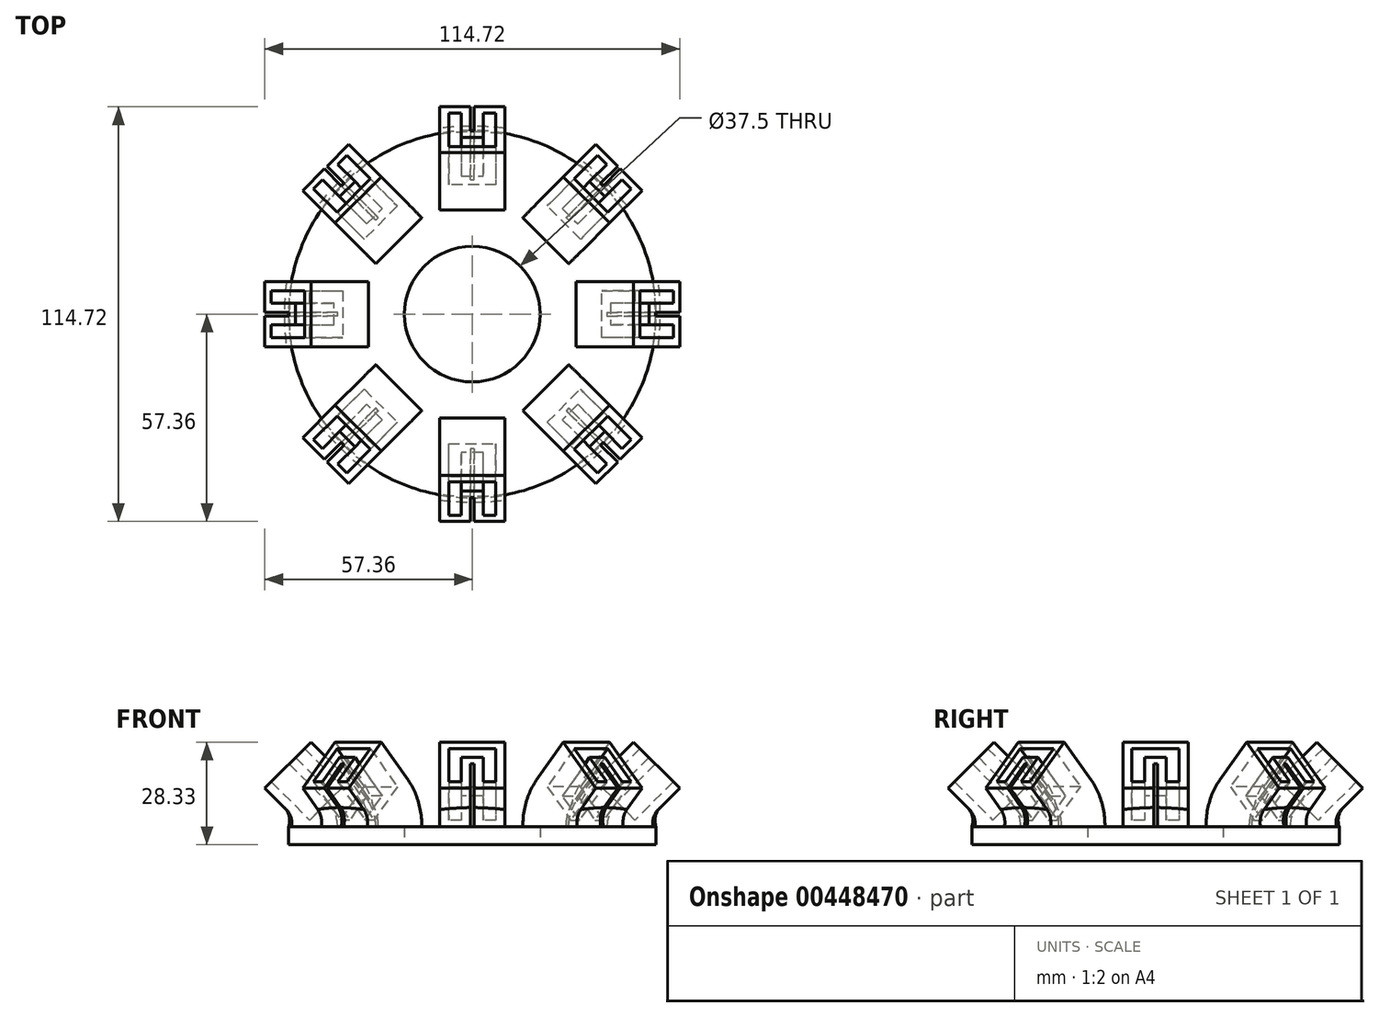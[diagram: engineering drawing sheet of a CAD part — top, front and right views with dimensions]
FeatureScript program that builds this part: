
annotation { "Feature Type Name" : "Feature", "Feature Type Description" : "" }
export const myFeature = defineFeature(function(context is Context, id is Id, definition is map)
    precondition{}
    {
        {
            var Q0;
            Q0=qCreatedBy(makeId("Top.planeOp"),FACE);
            var sketch = newSketch(context, id + "F0", { "sketchPlane" : qUnion([Q0])});
            skCircle(sketch, "E0", {"center": v(0, 0) * mm, "radius": 18.75 * mm});
            skCircle(sketch, "E1", {"center": v(0, 0) * mm, "radius": 50.8 * mm});
            skSolve(sketch);
        }
        {
            var Q0;
            Q0=makeQuery(id+"F0.imprint","IMPRINT",FACE,{"disambiguationData":[TD([[makeQuery(id+"F0.imprint","IMPRINT",EDGE,{"derivedFrom":sQuery(id+"F0.wireOp",EDGE,"E0")}),-1.0]])]});
            extrude(context, id + "F1", {"entities" : qUnion([Q0]), "depth" : 5 * mm});
        }
        {
            var Q0;
            Q0=makeQuery(id+"F1.opExtrude","CAP_FACE",FACE,{"disambiguationData":[OSD([sQuery(id+"F0.wireOp",EDGE,"E0"),sQuery(id+"F0.wireOp",EDGE,"E1")])],"isStart":false});
            var sketch = newSketch(context, id + "F2", { "sketchPlane" : qUnion([Q0])});
            skPoint(sketch, "E2", {"position": v(0, -31.75) * mm});
            skLineSegment(sketch, "E3", {"start": v(6, -31.75) * mm, "end": v(-6, -31.75) * mm});
            skLineSegment(sketch, "E4", {"start": v(6, -31.75) * mm, "end": v(6, -43.75) * mm});
            skLineSegment(sketch, "E5", {"start": v(-6, -31.75) * mm, "end": v(-6, -43.75) * mm});
            skLineSegment(sketch, "E6.0", {"start": v(-3.5, -34.25) * mm, "end": v(-3.5, -43.75) * mm});
            skLineSegment(sketch, "E6.1", {"start": v(3.5, -34.25) * mm, "end": v(-3.5, -34.25) * mm});
            skLineSegment(sketch, "E6.2", {"start": v(3.5, -34.25) * mm, "end": v(3.5, -43.75) * mm});
            skLineSegment(sketch, "E7", {"start": v(-6, -43.75) * mm, "end": v(-3.5, -43.75) * mm});
            skLineSegment(sketch, "E8", {"start": v(3.5, -43.75) * mm, "end": v(6, -43.75) * mm});
            skLineSegment(sketch, "E9.0", {"start": v(6.5, -31.25) * mm, "end": v(6.5, -44.25) * mm});
            skLineSegment(sketch, "E9.1", {"start": v(3, -44.25) * mm, "end": v(6.5, -44.25) * mm});
            skLineSegment(sketch, "E9.2", {"start": v(6.5, -31.25) * mm, "end": v(-6.5, -31.25) * mm});
            skLineSegment(sketch, "E9.3", {"start": v(3, -34.75) * mm, "end": v(3, -44.25) * mm});
            skLineSegment(sketch, "E9.4", {"start": v(-6.5, -31.25) * mm, "end": v(-6.5, -44.25) * mm});
            skLineSegment(sketch, "E9.5", {"start": v(-6.5, -44.25) * mm, "end": v(-3, -44.25) * mm});
            skLineSegment(sketch, "E9.6", {"start": v(-3, -34.75) * mm, "end": v(-3, -44.25) * mm});
            skLineSegment(sketch, "E9.7", {"start": v(3, -34.75) * mm, "end": v(-3, -34.75) * mm});
            skLineSegment(sketch, "E10.0", {"start": v(9, -28.75) * mm, "end": v(9, -46.75) * mm});
            skLineSegment(sketch, "E10.1", {"start": v(0.5, -46.75) * mm, "end": v(9, -46.75) * mm});
            skLineSegment(sketch, "E10.2", {"start": v(9, -28.75) * mm, "end": v(-9, -28.75) * mm});
            skLineSegment(sketch, "E10.3", {"start": v(0.5, -37.25) * mm, "end": v(0.5, -46.75) * mm});
            skLineSegment(sketch, "E10.4", {"start": v(-9, -28.75) * mm, "end": v(-9, -46.75) * mm});
            skLineSegment(sketch, "E10.5", {"start": v(-9, -46.75) * mm, "end": v(-0.5, -46.75) * mm});
            skLineSegment(sketch, "E10.6", {"start": v(-0.5, -37.25) * mm, "end": v(-0.5, -46.75) * mm});
            skLineSegment(sketch, "E10.7", {"start": v(0.5, -37.25) * mm, "end": v(-0.5, -37.25) * mm});
            skSolve(sketch);
        }
        {
            var Q0;
            Q0=qCreatedBy(makeId("Right.planeOp"),FACE);
            var sketch = newSketch(context, id + "F3", { "sketchPlane" : qUnion([Q0])});
            skPoint(sketch, "E11", {"position": v(-28.75, 5) * mm});
            skLineSegment(sketch, "E12", {"start": v(-28.75, 5) * mm, "end": v(-46.75, 5) * mm, "construction": true});
            skArc(sketch, "E13", {"start": v(-28.75, 5) * mm, "mid": v(-30.12, 11.89) * mm, "end": v(-34.02, 17.73) * mm});
            skLineSegment(sketch, "E14", {"start": v(-46.75, 5) * mm, "end": v(-34.02, 17.73) * mm, "construction": true});
            skSolve(sketch);
        }
        {
            var Q0;
            Q0=makeQuery(id+"F2.imprint","IMPRINT",FACE,{"disambiguationData":[TD([[makeQuery(id+"F2.imprint","IMPRINT",EDGE,{"derivedFrom":sQuery(id+"F2.wireOp",EDGE,"E9.0")}),1.0]])]});
            var Q1;
            Q1=makeQuery(id+"F2.imprint","IMPRINT",FACE,{"disambiguationData":[TD([[makeQuery(id+"F2.imprint","IMPRINT",EDGE,{"derivedFrom":sQuery(id+"F2.wireOp",EDGE,"E3")}),-1.0]])]});
            var Q2;
            Q2=makeQuery(id+"F2.imprint","IMPRINT",FACE,{"disambiguationData":[TD([[makeQuery(id+"F2.imprint","IMPRINT",EDGE,{"derivedFrom":sQuery(id+"F2.wireOp",EDGE,"E3")}),1.0]])]});
            var Q3;
            Q3=sQuery(id+"F3.wireOp",EDGE,"E13");
            sweep(context, id + "F4", {"operationType" : NewBodyOperationType.ADD, "profiles" : qUnion([Q0, Q1, Q2]), "path" : qUnion([Q3])});
        }
        {
            var Q0;
            Q0=makeQuery(id+"F4.opSweep","CAP_FACE",FACE,{"disambiguationData":[OSD([sQuery(id+"F2.wireOp",EDGE,"E10.0"),sQuery(id+"F2.wireOp",EDGE,"E10.1"),sQuery(id+"F2.wireOp",EDGE,"E10.2"),sQuery(id+"F2.wireOp",EDGE,"E10.3"),sQuery(id+"F2.wireOp",EDGE,"E10.4"),sQuery(id+"F2.wireOp",EDGE,"E10.5"),sQuery(id+"F2.wireOp",EDGE,"E10.6"),sQuery(id+"F2.wireOp",EDGE,"E10.7"),sQuery(id+"F3.wireOp",VERTEX,"E13.end")])],"isStart":false});
            var sketch = newSketch(context, id + "F5", { "sketchPlane" : qUnion([Q0])});
            skLineSegment(sketch, "E15", {"start": v(-9, -29.52) * mm, "end": v(-9, -11.52) * mm});
            skLineSegment(sketch, "E16", {"start": v(-9, -11.52) * mm, "end": v(9, -11.52) * mm});
            skLineSegment(sketch, "E17", {"start": v(9, -11.52) * mm, "end": v(9, -29.52) * mm});
            skLineSegment(sketch, "E18", {"start": v(9, -29.52) * mm, "end": v(0.5, -29.52) * mm});
            skLineSegment(sketch, "E19", {"start": v(0.5, -29.52) * mm, "end": v(0.5, -20.02) * mm});
            skLineSegment(sketch, "E20", {"start": v(0.5, -20.02) * mm, "end": v(-0.5, -20.02) * mm});
            skLineSegment(sketch, "E21", {"start": v(-0.5, -20.02) * mm, "end": v(-0.5, -29.52) * mm});
            skLineSegment(sketch, "E22", {"start": v(-0.5, -29.52) * mm, "end": v(-9, -29.52) * mm});
            skLineSegment(sketch, "E23.0", {"start": v(-6.5, -27.02) * mm, "end": v(-6.5, -14.02) * mm});
            skLineSegment(sketch, "E23.1", {"start": v(-3, -27.02) * mm, "end": v(-6.5, -27.02) * mm});
            skLineSegment(sketch, "E23.2", {"start": v(-6.5, -14.02) * mm, "end": v(6.5, -14.02) * mm});
            skLineSegment(sketch, "E23.3", {"start": v(-3, -17.52) * mm, "end": v(-3, -27.02) * mm});
            skLineSegment(sketch, "E23.4", {"start": v(6.5, -14.02) * mm, "end": v(6.5, -27.02) * mm});
            skLineSegment(sketch, "E23.5", {"start": v(6.5, -27.02) * mm, "end": v(3, -27.02) * mm});
            skLineSegment(sketch, "E23.6", {"start": v(3, -27.02) * mm, "end": v(3, -17.52) * mm});
            skLineSegment(sketch, "E23.7", {"start": v(3, -17.52) * mm, "end": v(-3, -17.52) * mm});
            skSolve(sketch);
        }
        {
            var Q0;
            Q0=makeQuery(id+"F5.imprint","IMPRINT",FACE,{"disambiguationData":[TD([[makeQuery(id+"F5.imprint","IMPRINT",EDGE,{"derivedFrom":sQuery(id+"F5.wireOp",EDGE,"E15")}),1.0]])]});
            extrude(context, id + "F6", {"entities" : qUnion([Q0]), "operationType" : NewBodyOperationType.ADD, "depth" : 15 * mm});
        }
        {
            var Q0;
            Q0=makeQuery(id+"F6.boolean.opBoolean","MERGE",EDGE,{"derivedFrom":[makeQuery(id+"F4.opSweep","CAP_EDGE",EDGE,{"disambiguationData":[OSD([sQuery(id+"F2.wireOp",EDGE,"E10.5"),sQuery(id+"F3.wireOp",VERTEX,"E13.start"),sQuery(id+"F3.wireOp",VERTEX,"E13.end")])],"isStart":true}),makeQuery(id+"F6.opExtrude","CAP_EDGE",EDGE,{"disambiguationData":[OSD([sQuery(id+"F5.wireOp",EDGE,"E22")])],"isStart":true})]});
            var Q1;
            Q1=makeQuery(id+"F6.boolean.opBoolean","MERGE",EDGE,{"derivedFrom":[makeQuery(id+"F4.opSweep","CAP_EDGE",EDGE,{"disambiguationData":[OSD([sQuery(id+"F2.wireOp",EDGE,"E10.1"),sQuery(id+"F3.wireOp",VERTEX,"E13.start"),sQuery(id+"F3.wireOp",VERTEX,"E13.end")])],"isStart":true}),makeQuery(id+"F6.opExtrude","CAP_EDGE",EDGE,{"disambiguationData":[OSD([sQuery(id+"F5.wireOp",EDGE,"E18")])],"isStart":true})]});
            var Q2;
            Q2=makeQuery(id+"F4.opSweep","CAP_EDGE",EDGE,{"disambiguationData":[OSD([sQuery(id+"F2.wireOp",EDGE,"E10.4"),sQuery(id+"F3.wireOp",VERTEX,"E13.start")])],"isStart":true});
            var Q3;
            Q3=makeQuery(id+"F4.opSweep","CAP_EDGE",EDGE,{"disambiguationData":[OSD([sQuery(id+"F2.wireOp",EDGE,"E10.2"),sQuery(id+"F3.wireOp",VERTEX,"E13.start")])],"isStart":true});
            var Q4;
            Q4=makeQuery(id+"F4.opSweep","CAP_EDGE",EDGE,{"disambiguationData":[OSD([sQuery(id+"F2.wireOp",EDGE,"E10.0"),sQuery(id+"F3.wireOp",VERTEX,"E13.start")])],"isStart":true});
            fillet(context, id + "F7", {"entities" : qUnion([Q0, Q1, Q2, Q3, Q4]), "radius" : 5 * mm, "tangentPropagation" : true, "allowEdgeOverflow" : false});
        }
        {
            var Q0;
            Q0=qCreatedBy(makeId("Right.planeOp"),FACE);
            var sketch = newSketch(context, id + "F8", { "sketchPlane" : qUnion([Q0])});
            skLineSegment(sketch, "E24", {"start": v(0, 0) * mm, "end": v(0, 26.54) * mm, "construction": true});
            skSolve(sketch);
        }
        {
            var Q0;
            Q0=makeQuery(id+"F1.opExtrude","SWEPT_BODY",BODY,{"disambiguationData":[OSD([sQuery(id+"F0.wireOp",EDGE,"E0"),sQuery(id+"F0.wireOp",EDGE,"E1")])]});
            var Q1;
            Q1=sQuery(id+"F8.wireOp",EDGE,"E24");
            circularPattern(context, id + "F9", {"operationType" : NewBodyOperationType.ADD, "entities" : qUnion([Q0]), "axis" : qUnion([Q1]), "angle" : 360 * degree, "instanceCount" : 8, "equalSpace" : true});
        }
        {
            var Q0;
            Q0=qCreatedBy(makeId("Top.planeOp"),FACE);
            var Q1;
            Q1=makeQuery(id+"F9.opPattern","COPY",VERTEX,{"derivedFrom":makeQuery(id+"F6.opExtrude","CAP_VERTEX",VERTEX,{"disambiguationData":[OSD([sQuery(id+"F5.wireOp",EDGE,"E23.4"),sQuery(id+"F5.wireOp",EDGE,"E23.5")])],"isStart":false}),"instanceName":"1"});
            cPlane(context, id + "F10", {"entities" : qUnion([Q0, Q1]), "cplaneType" : CPlaneType.PLANE_POINT, "offset" : 25 * mm, "width" : 150 * mm, "height" : 150 * mm});
        }
    });
